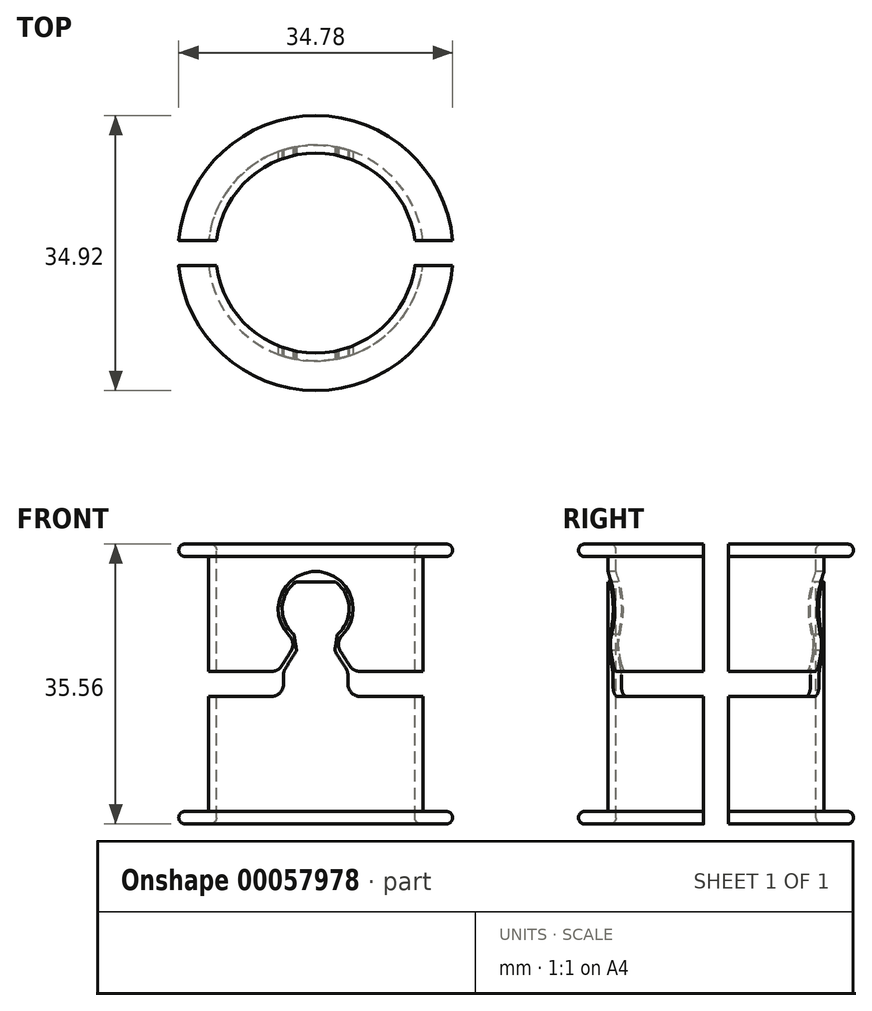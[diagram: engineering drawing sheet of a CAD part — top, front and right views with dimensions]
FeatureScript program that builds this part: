
annotation { "Feature Type Name" : "Feature", "Feature Type Description" : "" }
export const myFeature = defineFeature(function(context is Context, id is Id, definition is map)
    precondition{}
    {
        {
            var Q0;
            Q0=qCreatedBy(makeId("Right.planeOp"),FACE);
            var sketch = newSketch(context, id + "F0", { "sketchPlane" : qUnion([Q0])});
            skLineSegment(sketch, "E0", {"start": v(0, 17.78) * mm, "end": v(0, -17.78) * mm, "construction": true});
            skLineSegment(sketch, "E1", {"start": v(-13.49, 17.78) * mm, "end": v(-16.68, 17.78) * mm});
            skLineSegment(sketch, "E2", {"start": v(-17.46, 17) * mm, "end": v(-17.46, 16.98) * mm});
            skLineSegment(sketch, "E3", {"start": v(-16.68, 16.2) * mm, "end": v(-13.72, 16.2) * mm});
            skLineSegment(sketch, "E4", {"start": v(-13.72, 16.2) * mm, "end": v(-13.72, -16.2) * mm});
            skLineSegment(sketch, "E5", {"start": v(-13.72, -16.2) * mm, "end": v(-16.68, -16.2) * mm});
            skLineSegment(sketch, "E6", {"start": v(-17.46, -16.98) * mm, "end": v(-17.46, -17) * mm});
            skLineSegment(sketch, "E7", {"start": v(-16.68, -17.78) * mm, "end": v(-13.49, -17.78) * mm});
            skLineSegment(sketch, "E8", {"start": v(-12.7, 17) * mm, "end": v(-12.7, -17) * mm});
            skPoint(sketch, "E9.visualSharp", {"position": v(-12.7, 17.78) * mm});
            skArc(sketch, "E9.filletArc", {"start": v(-12.7, 17) * mm, "mid": v(-12.93, 17.55) * mm, "end": v(-13.49, 17.78) * mm});
            skPoint(sketch, "E10.visualSharp", {"position": v(-17.46, 17.78) * mm});
            skArc(sketch, "E10.filletArc", {"start": v(-16.68, 17.78) * mm, "mid": v(-17.23, 17.55) * mm, "end": v(-17.46, 17) * mm});
            skPoint(sketch, "E11.visualSharp", {"position": v(-17.46, 16.2) * mm});
            skArc(sketch, "E11.filletArc", {"start": v(-17.46, 16.98) * mm, "mid": v(-17.23, 16.42) * mm, "end": v(-16.68, 16.2) * mm});
            skPoint(sketch, "E12.visualSharp", {"position": v(-12.7, -17.78) * mm});
            skArc(sketch, "E12.filletArc", {"start": v(-13.49, -17.78) * mm, "mid": v(-12.93, -17.55) * mm, "end": v(-12.7, -17) * mm});
            skPoint(sketch, "E13.visualSharp", {"position": v(-17.46, -17.78) * mm});
            skArc(sketch, "E13.filletArc", {"start": v(-17.46, -17) * mm, "mid": v(-17.23, -17.55) * mm, "end": v(-16.68, -17.78) * mm});
            skPoint(sketch, "E14.visualSharp", {"position": v(-17.46, -16.2) * mm});
            skArc(sketch, "E14.filletArc", {"start": v(-16.68, -16.2) * mm, "mid": v(-17.23, -16.42) * mm, "end": v(-17.46, -16.98) * mm});
            skSolve(sketch);
        }
        {
            var Q0;
            Q0=makeQuery(id+"F0.imprint","IMPRINT",FACE,{"disambiguationData":[TD([[makeQuery(id+"F0.imprint","IMPRINT",EDGE,{"derivedFrom":sQuery(id+"F0.wireOp",EDGE,"E1")}),1.0]])]});
            var Q1;
            Q1=sQuery(id+"F0.wireOp",EDGE,"E0");
            revolve(context, id + "F1", {"entities" : qUnion([Q0]), "axis" : qUnion([Q1]), "revolveType" : RevolveType.FULL});
        }
        {
            var Q0;
            Q0=qCreatedBy(makeId("Top.planeOp"),FACE);
            var sketch = newSketch(context, id + "F2", { "sketchPlane" : qUnion([Q0])});
            skLineSegment(sketch, "E15.rect.bottom", {"start": v(-25.4, 1.59) * mm, "end": v(25.4, 1.59) * mm});
            skLineSegment(sketch, "E15.rect.top", {"start": v(-25.4, -1.59) * mm, "end": v(25.4, -1.59) * mm});
            skLineSegment(sketch, "E15.rect.left", {"start": v(-25.4, 1.59) * mm, "end": v(-25.4, -1.59) * mm});
            skLineSegment(sketch, "E15.rect.right", {"start": v(25.4, 1.59) * mm, "end": v(25.4, -1.59) * mm});
            skPoint(sketch, "E15.rect.middle", {"position": v(0, 0) * mm});
            skSolve(sketch);
        }
        {
            var Q0;
            Q0=qSketchRegion(id+"F2",true);
            extrude(context, id + "F3", {"entities" : qUnion([Q0]), "operationType" : NewBodyOperationType.REMOVE, "endBound" : BoundingType.SYMMETRIC, "oppositeDirection" : true, "depth" : 50.8 * mm});
        }
        {
            var Q0;
            Q0=qCreatedBy(makeId("Front.planeOp"),FACE);
            var sketch = newSketch(context, id + "F4", { "sketchPlane" : qUnion([Q0])});
            skLineSegment(sketch, "E16.rect.bottom", {"start": v(25.4, 1.59) * mm, "end": v(5.63, 1.59) * mm});
            skLineSegment(sketch, "E16.rect.top", {"start": v(25.4, -1.59) * mm, "end": v(5.66, -1.59) * mm});
            skLineSegment(sketch, "E16.rect.left", {"start": v(25.4, 1.59) * mm, "end": v(25.4, -1.59) * mm});
            skLineSegment(sketch, "E16.rect.right", {"start": v(-25.4, 1.59) * mm, "end": v(-25.4, -1.59) * mm});
            skPoint(sketch, "E16.rect.middle", {"position": v(0, 0) * mm});
            skArc(sketch, "E17", {"start": v(3.36, 6.15) * mm, "mid": v(0, 14.29) * mm, "end": v(-3.36, 6.15) * mm});
            skPoint(sketch, "E17.centerSnap0", {"position": v(0, 1.59) * mm});
            skLineSegment(sketch, "E18", {"start": v(-2.37, 5.4) * mm, "end": v(2.37, 5.4) * mm, "construction": true});
            skLineSegment(sketch, "E19", {"start": v(-4.76, 9.53) * mm, "end": v(-4.76, 1.59) * mm, "construction": true});
            skLineSegment(sketch, "E20", {"start": v(4.76, 9.53) * mm, "end": v(4.76, 1.59) * mm, "construction": true});
            skLineSegment(sketch, "E21", {"start": v(-3.13, 4.2) * mm, "end": v(-4.3, 2.33) * mm});
            skLineSegment(sketch, "E22", {"start": v(3.13, 4.2) * mm, "end": v(4.3, 2.33) * mm});
            skLineSegment(sketch, "E23.trimOffspring", {"start": v(-5.63, 1.59) * mm, "end": v(-25.4, 1.59) * mm});
            skArc(sketch, "E24", {"start": v(2.75, 6.28) * mm, "mid": v(4.25, 9.67) * mm, "end": v(2.52, 12.95) * mm});
            skLineSegment(sketch, "E25", {"start": v(-1.59, 5.58) * mm, "end": v(1.59, 5.58) * mm, "construction": true});
            skLineSegment(sketch, "E26", {"start": v(-2.43, 4.24) * mm, "end": v(-3.85, 1.97) * mm});
            skLineSegment(sketch, "E27", {"start": v(-4.09, 1.13) * mm, "end": v(-4.09, -0.01) * mm});
            skLineSegment(sketch, "E28", {"start": v(2.43, 4.24) * mm, "end": v(3.85, 1.97) * mm});
            skLineSegment(sketch, "E29", {"start": v(4.09, 1.13) * mm, "end": v(4.09, -0.01) * mm});
            skLineSegment(sketch, "E30.trimOffspring", {"start": v(-5.66, -1.59) * mm, "end": v(-25.4, -1.59) * mm});
            skPoint(sketch, "E31.visualSharp", {"position": v(-1.59, 5.58) * mm});
            skPoint(sketch, "E32.visualSharp", {"position": v(1.59, 5.58) * mm});
            skPoint(sketch, "E33.visualSharp", {"position": v(2.37, 5.4) * mm});
            skArc(sketch, "E33.filletArc", {"start": v(3.36, 6.15) * mm, "mid": v(2.9, 5.2) * mm, "end": v(3.13, 4.2) * mm});
            skPoint(sketch, "E34.visualSharp", {"position": v(-2.37, 5.4) * mm});
            skArc(sketch, "E34.filletArc", {"start": v(-3.13, 4.2) * mm, "mid": v(-2.9, 5.2) * mm, "end": v(-3.36, 6.15) * mm});
            skPoint(sketch, "E35.visualSharp", {"position": v(-4.76, 1.59) * mm});
            skArc(sketch, "E35.filletArc", {"start": v(-5.63, 1.59) * mm, "mid": v(-4.87, 1.78) * mm, "end": v(-4.3, 2.33) * mm});
            skPoint(sketch, "E36.visualSharp", {"position": v(-4.09, 1.59) * mm});
            skArc(sketch, "E36.filletArc", {"start": v(-3.85, 1.97) * mm, "mid": v(-4.03, 1.57) * mm, "end": v(-4.09, 1.13) * mm});
            skPoint(sketch, "E37.visualSharp", {"position": v(4.09, 1.59) * mm});
            skArc(sketch, "E37.filletArc", {"start": v(4.09, 1.13) * mm, "mid": v(4.03, 1.57) * mm, "end": v(3.85, 1.97) * mm});
            skPoint(sketch, "E38.visualSharp", {"position": v(4.76, 1.59) * mm});
            skArc(sketch, "E38.filletArc", {"start": v(4.3, 2.33) * mm, "mid": v(4.87, 1.78) * mm, "end": v(5.63, 1.59) * mm});
            skPoint(sketch, "E39.visualSharp", {"position": v(-4.09, -1.59) * mm});
            skArc(sketch, "E39.filletArc", {"start": v(-5.66, -1.59) * mm, "mid": v(-4.55, -1.13) * mm, "end": v(-4.09, -0.01) * mm});
            skPoint(sketch, "E40.visualSharp", {"position": v(4.09, -1.59) * mm});
            skArc(sketch, "E40.filletArc", {"start": v(4.09, -0.01) * mm, "mid": v(4.55, -1.13) * mm, "end": v(5.66, -1.59) * mm});
            skLineSegment(sketch, "E41", {"start": v(-2.52, 12.95) * mm, "end": v(2.52, 12.95) * mm});
            skArc(sketch, "E42.trimOffspring", {"start": v(-2.52, 12.95) * mm, "mid": v(-4.25, 9.67) * mm, "end": v(-2.75, 6.28) * mm});
            skLineSegment(sketch, "E43", {"start": v(-2.75, 6.28) * mm, "end": v(-2.43, 4.24) * mm});
            skLineSegment(sketch, "E44", {"start": v(2.75, 6.28) * mm, "end": v(2.43, 4.24) * mm});
            skSolve(sketch);
        }
        {
            var Q0;
            Q0=makeQuery(id+"F4.imprint","IMPRINT",FACE,{"disambiguationData":[TD([[makeQuery(id+"F4.imprint","IMPRINT",EDGE,{"derivedFrom":sQuery(id+"F4.wireOp",EDGE,"E16.rect.bottom")}),1.0]])]});
            extrude(context, id + "F5", {"entities" : qUnion([Q0]), "operationType" : NewBodyOperationType.REMOVE, "endBound" : BoundingType.SYMMETRIC, "oppositeDirection" : true, "depth" : 50.8 * mm});
        }
    });
